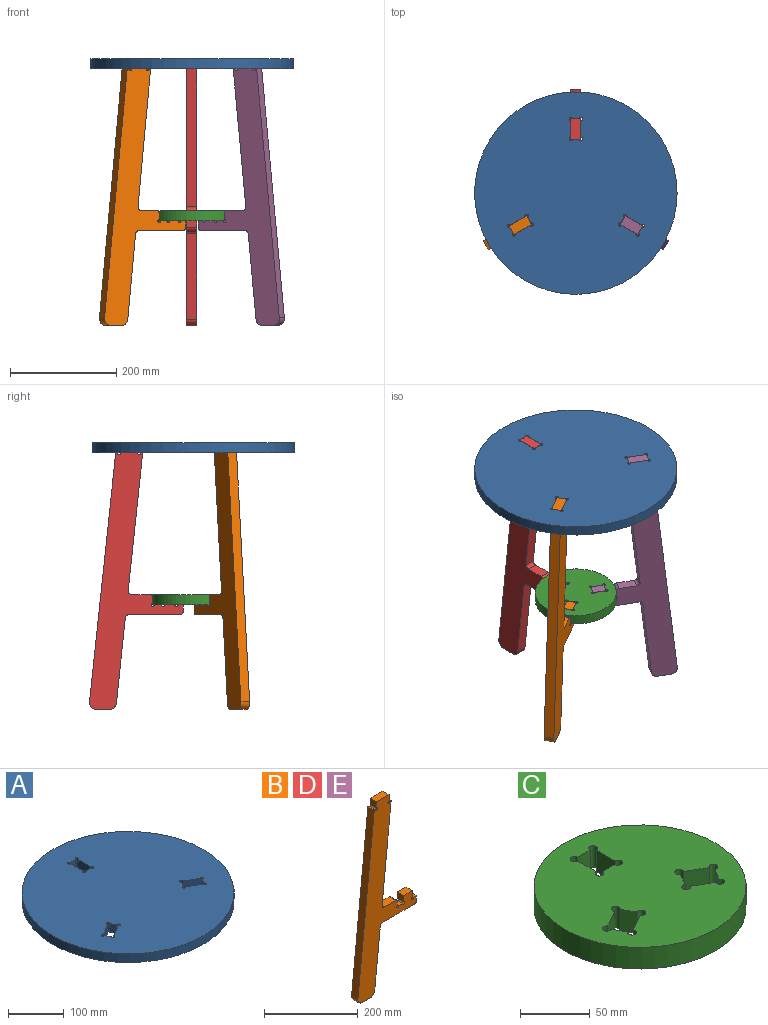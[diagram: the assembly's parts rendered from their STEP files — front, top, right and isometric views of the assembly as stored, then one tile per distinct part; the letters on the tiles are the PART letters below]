
ASSEMBLY  parts=5 mates=5
PART A: 27 faces, bbox 381x381x19.1 mm
  f0: plane 381x381mm, normal (0,0,-1), area 111546.7mm2, adj f1,f2,f3,f4,f5,f6,f7,f8
  f1: plane 27.5x19.05mm, normal (0.5,-0.87,0), area 604.8mm2, adj f0,f14,f16,f26
  f2: plane 19.05x11mm, normal (-0.87,-0.5,0), area 241.9mm2, adj f0,f14,f25,f26
  f3: plane 27.5x19.05mm, normal (-0.5,0.87,0), area 604.8mm2, adj f0,f14,f15,f25
  f4: plane 19.05x11mm, normal (0.87,-0.5,0), area 241.9mm2, adj f0,f14,f20,f24
  f5: plane 27.5x19.05mm, normal (-0.5,-0.87,0), area 604.8mm2, adj f0,f14,f23,f24
  f6: plane 19.05x11mm, normal (-0.87,0.5,0), area 241.9mm2, adj f0,f14,f19,f23
  f7: plane 31.75x19.05mm, normal (1,0,0), area 604.8mm2, adj f0,f14,f17,f22
  f8: plane 19.05x12.7mm, normal (0,-1,0), area 241.9mm2, adj f0,f14,f21,f22
  f9: plane 31.75x19.05mm, normal (-1,0,0), area 604.8mm2, adj f0,f14,f18,f21
  f10: cylinder r=190.5mm len=381mm, axis (0,0,-1), area 22801.8mm2, adj f0,f14
  f11: plane 27.5x19.05mm, normal (0.5,0.87,0), area 604.8mm2, adj f0,f14,f19,f20
  f12: plane 19.05x12.7mm, normal (0,1,0), area 241.9mm2, adj f0,f14,f17,f18
  f13: plane 19.05x11mm, normal (0.87,0.5,0), area 241.9mm2, adj f0,f14,f15,f16
  f14: plane 381x381mm, normal (0,0,1), area 111546.7mm2, adj f1,f2,f3,f4,f5,f6,f7,f8
  f15: cylinder r=3.17mm len=19.05mm, axis (0,0,1), area 285mm2, adj f0,f3,f13,f14
  f16: cylinder r=3.17mm len=19.05mm, axis (0,0,1), area 285mm2, adj f0,f1,f13,f14
  f17: cylinder r=3.17mm len=19.05mm, axis (0,0,1), area 285mm2, adj f0,f7,f12,f14
  f18: cylinder r=3.17mm len=19.05mm, axis (0,0,1), area 285mm2, adj f0,f9,f12,f14
  f19: cylinder r=3.17mm len=19.05mm, axis (0,0,1), area 285mm2, adj f0,f6,f11,f14
  f20: cylinder r=3.17mm len=19.05mm, axis (0,0,1), area 285mm2, adj f0,f4,f11,f14
  f21: cylinder r=3.17mm len=19.05mm, axis (0,0,1), area 285mm2, adj f0,f8,f9,f14
  f22: cylinder r=3.17mm len=19.05mm, axis (0,0,1), area 285mm2, adj f0,f7,f8,f14
  f23: cylinder r=3.17mm len=19.05mm, axis (0,0,1), area 285mm2, adj f0,f5,f6,f14
  f24: cylinder r=3.17mm len=19.05mm, axis (0,0,1), area 285mm2, adj f0,f4,f5,f14
  f25: cylinder r=3.17mm len=19.05mm, axis (0,0,1), area 285mm2, adj f0,f2,f3,f14
  f26: cylinder r=3.17mm len=19.05mm, axis (0,0,1), area 285mm2, adj f0,f1,f2,f14
PART B: 31 faces, bbox 176.4x19.1x501.7 mm
  f0: plane 501.65x176.4mm, normal (0,1,0), area 28498.1mm2, adj f1,f2,f3,f4,f5,f6,f7,f8
  f1: plane 19.05x12.7mm, normal (1,0,0), area 241.9mm2, adj f0,f2,f19,f23
  f2: plane 19.05x9.53mm, normal (0,0,1), area 181.5mm2, adj f0,f1,f19,f26
  f3: plane 19.05x15.88mm, normal (1,0,0), area 302.4mm2, adj f0,f4,f19,f26
  f4: plane 25.4x19.05mm, normal (0,0,1), area 483.9mm2, adj f0,f3,f5,f19
  f5: plane 19.05x15.88mm, normal (-1,0,0), area 302.4mm2, adj f0,f4,f19,f25
  f6: plane 19.05x12.7mm, normal (0,0,1), area 241.9mm2, adj f0,f19,f24,f25
  f7: plane 19.05x9.53mm, normal (1,0,0), area 181.5mm2, adj f0,f19,f20,f24
  f8: plane 33.76x19.05mm, normal (0,0,1), area 643mm2, adj f0,f19,f20,f21
  f9: plane 259.69x27.29mm, normal (0.99,0,-0.1), area 4974.3mm2, adj f0,f10,f19,f21
  f10: plane 19.05x3.18mm, normal (0,0,1), area 60.5mm2, adj f0,f9,f19,f30
  f11: plane 19.05x15.88mm, normal (1,0,0), area 302.4mm2, adj f0,f12,f19,f30
  f12: plane 38.1x19.05mm, normal (0,0,1), area 725.8mm2, adj f0,f11,f13,f19
  f13: plane 19.05x15.88mm, normal (-1,0,0), area 302.4mm2, adj f0,f12,f19,f29
  f14: plane 19.05x3.18mm, normal (0,0,1), area 60.5mm2, adj f0,f15,f19,f29
  f15: plane 468.57x49.25mm, normal (-0.99,0,0.1), area 8975.5mm2, adj f0,f14,f19,f27
  f16: plane 25.26x19.05mm, normal (0,0,-1), area 481.2mm2, adj f0,f19,f27,f28
  f17: plane 160.74x19.05mm, normal (0.99,0,-0.1), area 3079mm2, adj f0,f19,f22,f28
  f18: plane 96.25x19.05mm, normal (0,0,-1), area 1833.5mm2, adj f0,f19,f22,f23
  f19: plane 501.65x176.4mm, normal (0,-1,0), area 28498.1mm2, adj f1,f2,f3,f4,f5,f6,f7,f8
  f20: cylinder r=6.35mm len=19.05mm, axis (0,1,0), area 190mm2, adj f0,f7,f8,f19
  f21: cylinder r=6.35mm len=19.05mm, axis (0,1,0), area 202.7mm2, adj f0,f8,f9,f19
  f22: cylinder r=6.35mm len=19.05mm, axis (0,1,0), area 177.3mm2, adj f0,f17,f18,f19
  f23: cylinder r=6.35mm len=19.05mm, axis (0,1,0), area 190mm2, adj f0,f1,f18,f19
  f24: cylinder r=3.17mm len=19.05mm, axis (0,-1,0), area 285mm2, adj f0,f6,f7,f19
  f25: cylinder r=3.17mm len=19.05mm, axis (0,-1,0), area 285mm2, adj f0,f5,f6,f19
  f26: cylinder r=3.17mm len=19.05mm, axis (0,-1,0), area 285mm2, adj f0,f2,f3,f19
  f27: cylinder r=12.7mm len=19.05mm, axis (0,1,0), area 405.4mm2, adj f0,f15,f16,f19
  f28: cylinder r=12.7mm len=19.05mm, axis (0,1,0), area 354.7mm2, adj f0,f16,f17,f19
  f29: cylinder r=3.17mm len=19.05mm, axis (0,-1,0), area 285mm2, adj f0,f13,f14,f19
  f30: cylinder r=3.17mm len=19.05mm, axis (0,-1,0), area 285mm2, adj f0,f10,f11,f19
PART C: 27 faces, bbox 152.4x152.4x19.1 mm
  f0: plane 152.4x152.4mm, normal (0,0,-1), area 16504.8mm2, adj f2,f3,f4,f5,f6,f7,f8,f9
  f1: plane 152.4x152.4mm, normal (0,0,1), area 16504.8mm2, adj f2,f3,f4,f5,f6,f7,f8,f9
  f2: cylinder r=76.2mm len=152.4mm, axis (0,0,-1), area 9120.7mm2, adj f0,f1
  f3: plane 19.05x16.5mm, normal (0.5,-0.87,0), area 362.9mm2, adj f0,f1,f23,f26
  f4: plane 19.05x11mm, normal (0.87,0.5,0), area 241.9mm2, adj f0,f1,f25,f26
  f5: plane 19.05x16.5mm, normal (-0.5,0.87,0), area 362.9mm2, adj f0,f1,f24,f25
  f6: plane 19.05x11mm, normal (-0.87,-0.5,0), area 241.9mm2, adj f0,f1,f23,f24
  f7: plane 19.05x16.5mm, normal (-0.5,-0.87,0), area 362.9mm2, adj f0,f1,f19,f22
  f8: plane 19.05x11mm, normal (0.87,-0.5,0), area 241.9mm2, adj f0,f1,f21,f22
  f9: plane 19.05x16.5mm, normal (0.5,0.87,0), area 362.9mm2, adj f0,f1,f20,f21
  f10: plane 19.05x11mm, normal (-0.87,0.5,0), area 241.9mm2, adj f0,f1,f19,f20
  f11: plane 19.05x19.05mm, normal (1,0,0), area 362.9mm2, adj f0,f1,f17,f18
  f12: plane 19.05x12.7mm, normal (0,-1,0), area 241.9mm2, adj f0,f1,f15,f18
  f13: plane 19.05x12.7mm, normal (0,1,0), area 241.9mm2, adj f0,f1,f16,f17
  f14: plane 19.05x19.05mm, normal (-1,0,0), area 362.9mm2, adj f0,f1,f15,f16
  f15: cylinder r=3.17mm len=19.05mm, axis (0,0,1), area 285mm2, adj f0,f1,f12,f14
  f16: cylinder r=3.17mm len=19.05mm, axis (0,0,1), area 285mm2, adj f0,f1,f13,f14
  f17: cylinder r=3.17mm len=19.05mm, axis (0,0,1), area 285mm2, adj f0,f1,f11,f13
  f18: cylinder r=3.17mm len=19.05mm, axis (0,0,1), area 285mm2, adj f0,f1,f11,f12
  f19: cylinder r=3.17mm len=19.05mm, axis (0,0,1), area 285mm2, adj f0,f1,f7,f10
  f20: cylinder r=3.17mm len=19.05mm, axis (0,0,1), area 285mm2, adj f0,f1,f9,f10
  f21: cylinder r=3.17mm len=19.05mm, axis (0,0,1), area 285mm2, adj f0,f1,f8,f9
  f22: cylinder r=3.17mm len=19.05mm, axis (0,0,1), area 285mm2, adj f0,f1,f7,f8
  f23: cylinder r=3.17mm len=19.05mm, axis (0,0,1), area 285mm2, adj f0,f1,f3,f6
  f24: cylinder r=3.17mm len=19.05mm, axis (0,0,1), area 285mm2, adj f0,f1,f5,f6
  f25: cylinder r=3.17mm len=19.05mm, axis (0,0,1), area 285mm2, adj f0,f1,f4,f5
  f26: cylinder r=3.17mm len=19.05mm, axis (0,0,1), area 285mm2, adj f0,f1,f3,f4
PART D: same geometry as B
PART E: same geometry as B
PLACE A t=(0.49,-0.85,285.75)mm
PLACE B rot(axis=(0,0,1),30deg) t=(5.99,2.33,-196.85)mm
PLACE C t=(0.49,-0.85,0)mm
PLACE D rot(axis=(0,0,-1),90deg) t=(0.49,-7.2,-196.85)mm
PLACE E rot(axis=(0,0,1),150deg) t=(-5.01,2.33,-196.85)mm
MATE planar B.f4 <-> C.f2  axis (0,0,1) through (-38.01,-23.07,19.05)mm
MATE planar A.f10 <-> B.f12  axis (0,0,1) through (0.49,-0.85,304.8)mm
MATE cylindrical A.f10 <-> C.f2  axis (0,0,1) through (0.49,-0.85,304.8)mm
MATE planar B.f19 <-> C.f5  axis (0.5,-0.87,0) through (-22.25,-24.97,19.05)mm
MATE planar B.f3 <-> C.f6  axis (0.87,0.5,0) through (-27.01,-16.72,11.11)mm
